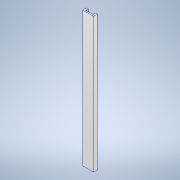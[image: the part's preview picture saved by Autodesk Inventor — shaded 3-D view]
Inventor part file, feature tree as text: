
AUTODESK INVENTOR PART (.ipt)
format: ipt  version: 2022 (Build 260153000, 153)  size: 103,936 bytes
history: native  units: mm
features: extrude x1, sketch x1
ambient origin geometry x8: Origin, YZ Plane, XZ Plane, XY Plane, X Axis, Y Axis, Z Axis, Center Point
bodies: Solid1 (feature_tree)
feature tree (2):
  extrude  "Extrusion1"  Depth=80.0mm
  sketch  "Sketch1"  dims[d0=15.0mm d1=80.0mm d2=1000.0mm d3=0.0mm]
